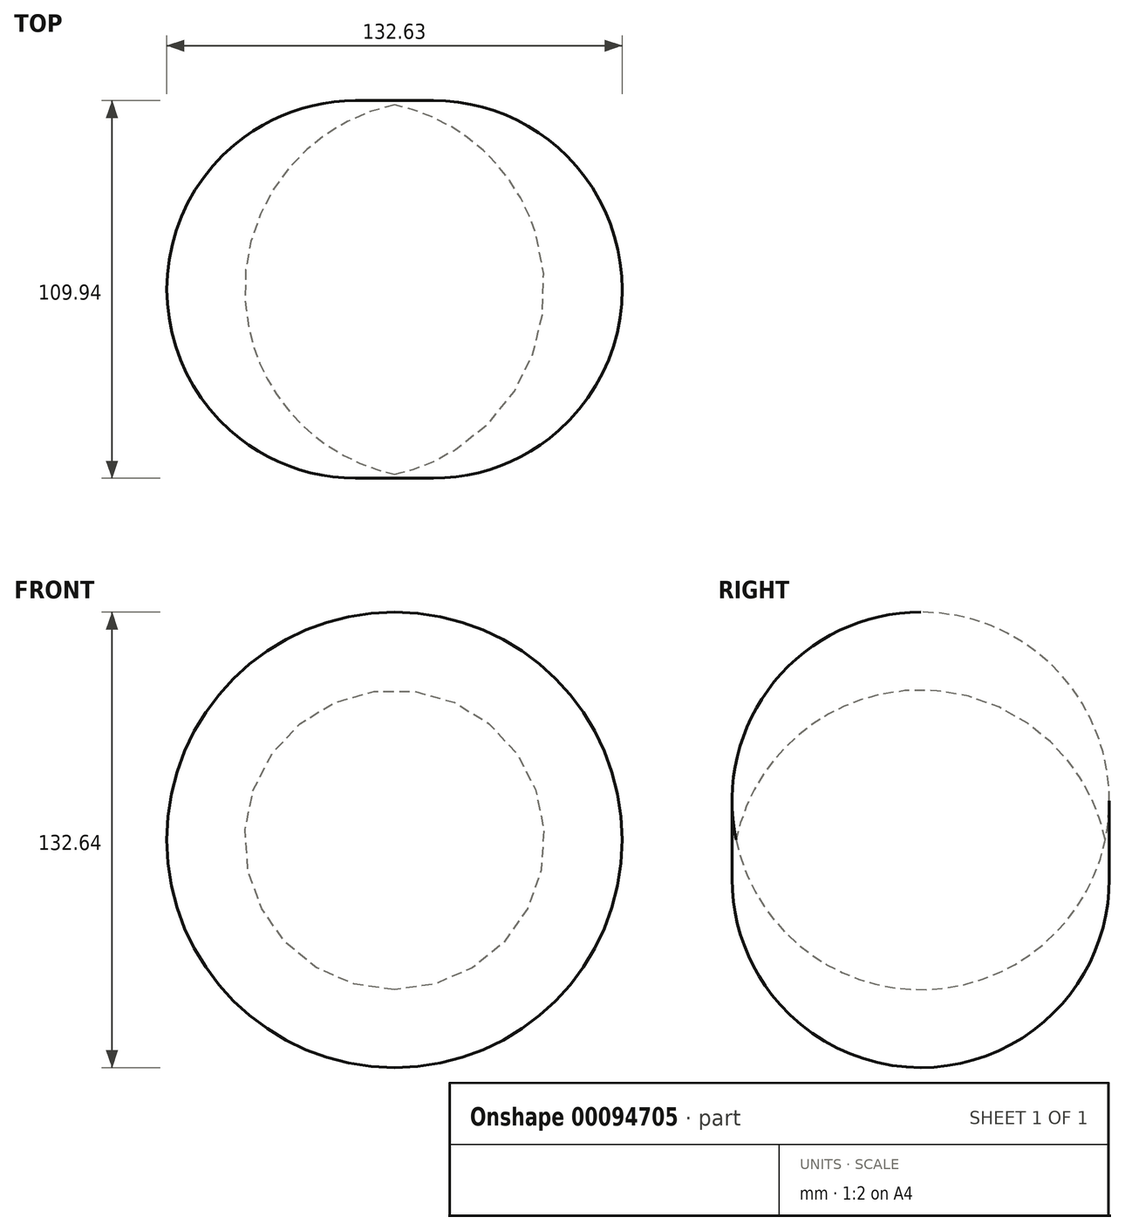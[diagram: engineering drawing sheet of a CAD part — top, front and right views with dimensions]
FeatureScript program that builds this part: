
annotation { "Feature Type Name" : "Feature", "Feature Type Description" : "" }
export const myFeature = defineFeature(function(context is Context, id is Id, definition is map)
    precondition{}
    {
        {
            var Q0;
            Q0=qCreatedBy(makeId("Top.planeOp"),FACE);
            var sketch = newSketch(context, id + "F0", { "sketchPlane" : qUnion([Q0])});
            skLineSegment(sketch, "E0", {"start": v(-49.76, 59.45) * mm, "end": v(-49.76, -48.13) * mm});
            skArc(sketch, "E1", {"start": v(-49.76, -48.13) * mm, "mid": v(16.55, 5.66) * mm, "end": v(-49.76, 59.45) * mm});
            skSolve(sketch);
        }
        {
            var Q0;
            Q0=makeQuery(id+"F0.imprint","IMPRINT",FACE,{"disambiguationData":[TD([[makeQuery(id+"F0.imprint","IMPRINT",EDGE,{"derivedFrom":sQuery(id+"F0.wireOp",EDGE,"E0")}),1.0]])]});
            var Q1;
            Q1=sQuery(id+"F0.wireOp",EDGE,"E0");
            revolve(context, id + "F1", {"entities" : qUnion([Q0]), "axis" : qUnion([Q1]), "revolveType" : RevolveType.FULL});
        }
    });
